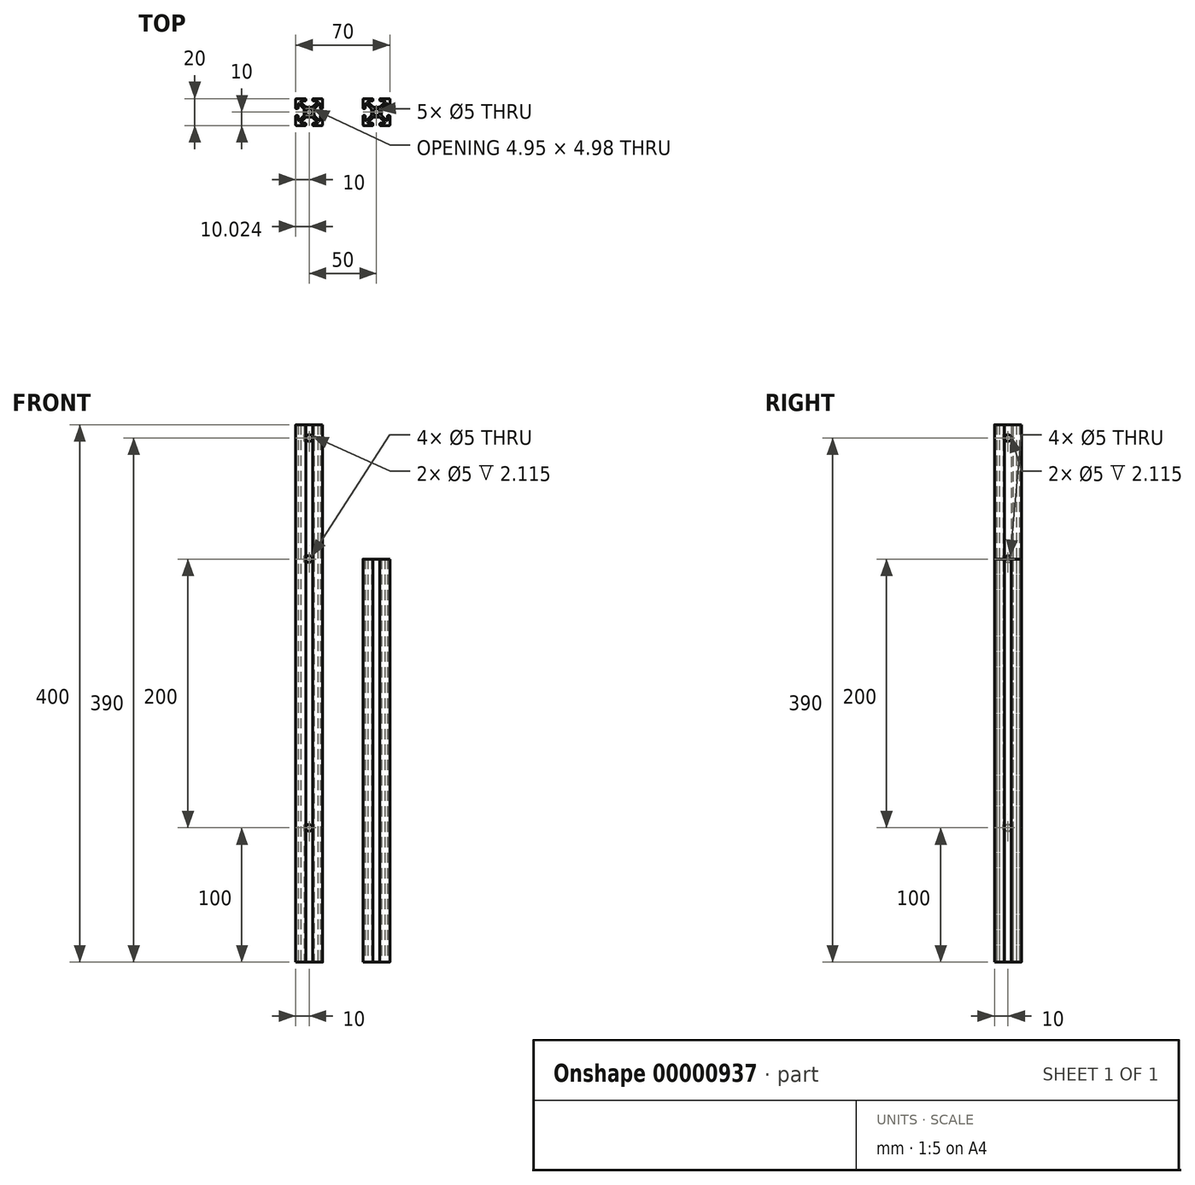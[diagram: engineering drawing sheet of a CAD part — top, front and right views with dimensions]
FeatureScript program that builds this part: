
annotation { "Feature Type Name" : "Feature", "Feature Type Description" : "" }
export const myFeature = defineFeature(function(context is Context, id is Id, definition is map)
    precondition{}
    {
        {
            var Q0;
            Q0=qCreatedBy(makeId("Top.planeOp"),FACE);
            var sketch = newSketch(context, id + "F0", { "sketchPlane" : qUnion([Q0])});
            skCircle(sketch, "E0", {"center": v(0, 0) * mm, "radius": 2.5 * mm});
            skLineSegment(sketch, "E1.bottom", {"start": v(-10, 10) * mm, "end": v(10, 10) * mm, "construction": true});
            skLineSegment(sketch, "E1.top", {"start": v(-10, -10) * mm, "end": v(10, -10) * mm, "construction": true});
            skLineSegment(sketch, "E1.left", {"start": v(-10, 10) * mm, "end": v(-10, -10) * mm, "construction": true});
            skLineSegment(sketch, "E1.right", {"start": v(10, 10) * mm, "end": v(10, -10) * mm, "construction": true});
            skLineSegment(sketch, "E2", {"start": v(-10, 10) * mm, "end": v(10, -10) * mm, "construction": true});
            skLineSegment(sketch, "E3", {"start": v(10, 10) * mm, "end": v(-10, -10) * mm, "construction": true});
            skLineSegment(sketch, "E4.rect.bottom", {"start": v(3.7, -3.7) * mm, "end": v(-3.7, -3.7) * mm, "construction": true});
            skLineSegment(sketch, "E4.rect.top", {"start": v(3.7, 3.7) * mm, "end": v(-3.7, 3.7) * mm, "construction": true});
            skLineSegment(sketch, "E4.rect.left", {"start": v(3.7, -3.7) * mm, "end": v(3.7, 3.7) * mm, "construction": true});
            skLineSegment(sketch, "E4.rect.right", {"start": v(-3.7, -3.7) * mm, "end": v(-3.7, 3.7) * mm, "construction": true});
            skLineSegment(sketch, "E5.rect.bottom", {"start": v(8.3, -8.3) * mm, "end": v(-8.3, -8.3) * mm, "construction": true});
            skLineSegment(sketch, "E5.rect.left", {"start": v(8.3, -8.3) * mm, "end": v(8.3, 8.3) * mm, "construction": true});
            skLineSegment(sketch, "E5.rect.right", {"start": v(-8.3, -8.3) * mm, "end": v(-8.3, 8.3) * mm, "construction": true});
            skLineSegment(sketch, "E6.rect.bottom", {"start": v(-2.5, 10) * mm, "end": v(2.5, 10) * mm, "construction": true});
            skLineSegment(sketch, "E6.rect.top", {"start": v(-2.5, -10) * mm, "end": v(2.5, -10) * mm, "construction": true});
            skLineSegment(sketch, "E6.rect.left", {"start": v(-2.5, 10) * mm, "end": v(-2.5, -10) * mm, "construction": true});
            skLineSegment(sketch, "E6.rect.right", {"start": v(2.5, 10) * mm, "end": v(2.5, -10) * mm, "construction": true});
            skLineSegment(sketch, "E7.rect.bottom", {"start": v(10, 2.5) * mm, "end": v(-10, 2.5) * mm, "construction": true});
            skLineSegment(sketch, "E7.rect.top", {"start": v(10, -2.5) * mm, "end": v(-10, -2.5) * mm, "construction": true});
            skLineSegment(sketch, "E7.rect.left", {"start": v(10, 2.5) * mm, "end": v(10, -2.5) * mm, "construction": true});
            skLineSegment(sketch, "E7.rect.right", {"start": v(-10, 2.5) * mm, "end": v(-10, -2.5) * mm, "construction": true});
            skLineSegment(sketch, "E8", {"start": v(-8.3, -7.1) * mm, "end": v(7.1, 8.3) * mm, "construction": true});
            skLineSegment(sketch, "E9", {"start": v(7.1, 8.3) * mm, "end": v(8.3, 7.1) * mm, "construction": true});
            skLineSegment(sketch, "E10", {"start": v(8.3, 7.1) * mm, "end": v(-7.1, -8.3) * mm, "construction": true});
            skLineSegment(sketch, "E11", {"start": v(-7.1, -8.3) * mm, "end": v(-8.3, -7.1) * mm, "construction": true});
            skLineSegment(sketch, "E12", {"start": v(-8.3, 7.1) * mm, "end": v(7.1, -8.3) * mm, "construction": true});
            skLineSegment(sketch, "E13", {"start": v(7.1, -8.3) * mm, "end": v(8.3, -7.1) * mm, "construction": true});
            skLineSegment(sketch, "E14", {"start": v(8.3, -7.1) * mm, "end": v(-7.1, 8.3) * mm, "construction": true});
            skLineSegment(sketch, "E15", {"start": v(-7.1, 8.3) * mm, "end": v(-8.3, 7.1) * mm, "construction": true});
            skLineSegment(sketch, "E16", {"start": v(-9.5, 2.5) * mm, "end": v(-8.8, 2.5) * mm});
            skLineSegment(sketch, "E17", {"start": v(-7.45, 6.24) * mm, "end": v(-4.29, 3.09) * mm});
            skLineSegment(sketch, "E18", {"start": v(-3.7, 1.67) * mm, "end": v(-3.7, -1.67) * mm});
            skLineSegment(sketch, "E19", {"start": v(-4.29, -3.08) * mm, "end": v(-7.45, -6.24) * mm});
            skLineSegment(sketch, "E20", {"start": v(-8.8, -2.5) * mm, "end": v(-9.5, -2.5) * mm});
            skLineSegment(sketch, "E21", {"start": v(-8.3, 3) * mm, "end": v(-8.3, 5.9) * mm});
            skLineSegment(sketch, "E22", {"start": v(-8.3, -5.9) * mm, "end": v(-8.3, -3) * mm});
            skLineSegment(sketch, "E23", {"start": v(-10, -3) * mm, "end": v(-10, -9.5) * mm});
            skLineSegment(sketch, "E24", {"start": v(-9.5, -10) * mm, "end": v(-3, -10) * mm});
            skLineSegment(sketch, "E25", {"start": v(-2.5, -9.5) * mm, "end": v(-2.5, -8.8) * mm});
            skLineSegment(sketch, "E26", {"start": v(-3, -8.3) * mm, "end": v(-5.89, -8.3) * mm});
            skLineSegment(sketch, "E27", {"start": v(-6.24, -7.45) * mm, "end": v(-3.09, -4.29) * mm});
            skLineSegment(sketch, "E28", {"start": v(-1.67, -3.7) * mm, "end": v(1.67, -3.7) * mm});
            skLineSegment(sketch, "E29", {"start": v(3.09, -4.29) * mm, "end": v(6.24, -7.45) * mm});
            skLineSegment(sketch, "E30", {"start": v(5.89, -8.3) * mm, "end": v(3, -8.3) * mm});
            skLineSegment(sketch, "E31", {"start": v(2.5, -8.8) * mm, "end": v(2.5, -9.5) * mm});
            skLineSegment(sketch, "E32", {"start": v(3, -10) * mm, "end": v(9.5, -10) * mm});
            skLineSegment(sketch, "E33", {"start": v(10, -9.5) * mm, "end": v(10, -3) * mm});
            skLineSegment(sketch, "E34", {"start": v(9.5, -2.5) * mm, "end": v(8.8, -2.5) * mm});
            skLineSegment(sketch, "E35", {"start": v(8.3, -3) * mm, "end": v(8.3, -5.89) * mm});
            skLineSegment(sketch, "E36", {"start": v(7.45, -6.24) * mm, "end": v(4.29, -3.09) * mm});
            skLineSegment(sketch, "E37", {"start": v(3.7, -1.67) * mm, "end": v(3.7, 1.67) * mm});
            skLineSegment(sketch, "E38", {"start": v(4.29, 3.09) * mm, "end": v(7.45, 6.24) * mm});
            skLineSegment(sketch, "E39", {"start": v(8.3, 5.89) * mm, "end": v(8.3, 3) * mm});
            skLineSegment(sketch, "E40", {"start": v(8.8, 2.5) * mm, "end": v(9.5, 2.5) * mm});
            skLineSegment(sketch, "E41", {"start": v(10, 3) * mm, "end": v(10, 9.5) * mm});
            skLineSegment(sketch, "E42", {"start": v(9.5, 10) * mm, "end": v(3, 10) * mm});
            skLineSegment(sketch, "E43", {"start": v(2.5, 9.5) * mm, "end": v(2.5, 8.8) * mm});
            skLineSegment(sketch, "E44", {"start": v(3, 8.3) * mm, "end": v(5.89, 8.3) * mm});
            skLineSegment(sketch, "E45", {"start": v(6.24, 7.45) * mm, "end": v(3.09, 4.29) * mm});
            skLineSegment(sketch, "E46", {"start": v(1.67, 3.7) * mm, "end": v(-1.67, 3.7) * mm});
            skLineSegment(sketch, "E47", {"start": v(-3.09, 4.29) * mm, "end": v(-6.24, 7.45) * mm});
            skLineSegment(sketch, "E48", {"start": v(-5.89, 8.3) * mm, "end": v(-3, 8.3) * mm});
            skLineSegment(sketch, "E49", {"start": v(-2.5, 8.8) * mm, "end": v(-2.5, 9.5) * mm});
            skLineSegment(sketch, "E50", {"start": v(-3, 10) * mm, "end": v(-9.5, 10) * mm});
            skLineSegment(sketch, "E51", {"start": v(-10, 9.5) * mm, "end": v(-10, 3) * mm});
            skPoint(sketch, "E52.visualSharp", {"position": v(-7.1, 8.3) * mm});
            skArc(sketch, "E52.filletArc", {"start": v(-5.89, 8.3) * mm, "mid": v(-6.35, 8) * mm, "end": v(-6.24, 7.45) * mm});
            skPoint(sketch, "E53.visualSharp", {"position": v(-8.3, 7.1) * mm});
            skArc(sketch, "E53.filletArc", {"start": v(-7.45, 6.24) * mm, "mid": v(-8, 6.35) * mm, "end": v(-8.3, 5.9) * mm});
            skPoint(sketch, "E54.visualSharp", {"position": v(-8.3, -7.1) * mm});
            skArc(sketch, "E54.filletArc", {"start": v(-8.3, -5.9) * mm, "mid": v(-8, -6.35) * mm, "end": v(-7.45, -6.24) * mm});
            skPoint(sketch, "E55.visualSharp", {"position": v(-7.1, -8.3) * mm});
            skArc(sketch, "E55.filletArc", {"start": v(-6.24, -7.45) * mm, "mid": v(-6.35, -8) * mm, "end": v(-5.89, -8.3) * mm});
            skPoint(sketch, "E56.visualSharp", {"position": v(7.1, -8.3) * mm});
            skArc(sketch, "E56.filletArc", {"start": v(5.89, -8.3) * mm, "mid": v(6.35, -8) * mm, "end": v(6.24, -7.45) * mm});
            skPoint(sketch, "E57.visualSharp", {"position": v(8.3, -7.1) * mm});
            skArc(sketch, "E57.filletArc", {"start": v(7.45, -6.24) * mm, "mid": v(8, -6.35) * mm, "end": v(8.3, -5.89) * mm});
            skPoint(sketch, "E58.visualSharp", {"position": v(8.3, 7.1) * mm});
            skArc(sketch, "E58.filletArc", {"start": v(8.3, 5.89) * mm, "mid": v(8, 6.35) * mm, "end": v(7.45, 6.24) * mm});
            skPoint(sketch, "E59.visualSharp", {"position": v(7.1, 8.3) * mm});
            skArc(sketch, "E59.filletArc", {"start": v(6.24, 7.45) * mm, "mid": v(6.35, 8) * mm, "end": v(5.89, 8.3) * mm});
            skPoint(sketch, "E60.visualSharp", {"position": v(-10, 10) * mm});
            skArc(sketch, "E60.filletArc", {"start": v(-9.5, 10) * mm, "mid": v(-9.85, 9.85) * mm, "end": v(-10, 9.5) * mm});
            skPoint(sketch, "E61.visualSharp", {"position": v(10, 10) * mm});
            skArc(sketch, "E61.filletArc", {"start": v(10, 9.5) * mm, "mid": v(9.85, 9.85) * mm, "end": v(9.5, 10) * mm});
            skPoint(sketch, "E62.visualSharp", {"position": v(10, -10) * mm});
            skArc(sketch, "E62.filletArc", {"start": v(9.5, -10) * mm, "mid": v(9.85, -9.85) * mm, "end": v(10, -9.5) * mm});
            skPoint(sketch, "E63.visualSharp", {"position": v(-10, -10) * mm});
            skArc(sketch, "E63.filletArc", {"start": v(-10, -9.5) * mm, "mid": v(-9.85, -9.85) * mm, "end": v(-9.5, -10) * mm});
            skPoint(sketch, "E64.visualSharp", {"position": v(-10, 2.5) * mm});
            skArc(sketch, "E64.filletArc", {"start": v(-10, 3) * mm, "mid": v(-9.85, 2.65) * mm, "end": v(-9.5, 2.5) * mm});
            skPoint(sketch, "E65.visualSharp", {"position": v(-2.5, 8.3) * mm});
            skArc(sketch, "E65.filletArc", {"start": v(-3, 8.3) * mm, "mid": v(-2.65, 8.45) * mm, "end": v(-2.5, 8.8) * mm});
            skPoint(sketch, "E66.visualSharp", {"position": v(-8.3, -2.5) * mm});
            skArc(sketch, "E66.filletArc", {"start": v(-8.3, -3) * mm, "mid": v(-8.45, -2.65) * mm, "end": v(-8.8, -2.5) * mm});
            skPoint(sketch, "E67.visualSharp", {"position": v(-2.5, 10) * mm});
            skArc(sketch, "E67.filletArc", {"start": v(-2.5, 9.5) * mm, "mid": v(-2.65, 9.85) * mm, "end": v(-3, 10) * mm});
            skPoint(sketch, "E68.visualSharp", {"position": v(2.5, 10) * mm});
            skArc(sketch, "E68.filletArc", {"start": v(3, 10) * mm, "mid": v(2.65, 9.85) * mm, "end": v(2.5, 9.5) * mm});
            skPoint(sketch, "E69.visualSharp", {"position": v(2.5, 8.3) * mm});
            skArc(sketch, "E69.filletArc", {"start": v(2.5, 8.8) * mm, "mid": v(2.65, 8.45) * mm, "end": v(3, 8.3) * mm});
            skPoint(sketch, "E70.visualSharp", {"position": v(8.3, 2.5) * mm});
            skArc(sketch, "E70.filletArc", {"start": v(8.3, 3) * mm, "mid": v(8.45, 2.65) * mm, "end": v(8.8, 2.5) * mm});
            skPoint(sketch, "E71.visualSharp", {"position": v(10, 2.5) * mm});
            skArc(sketch, "E71.filletArc", {"start": v(9.5, 2.5) * mm, "mid": v(9.85, 2.65) * mm, "end": v(10, 3) * mm});
            skPoint(sketch, "E72.visualSharp", {"position": v(8.3, -2.5) * mm});
            skArc(sketch, "E72.filletArc", {"start": v(8.8, -2.5) * mm, "mid": v(8.45, -2.65) * mm, "end": v(8.3, -3) * mm});
            skPoint(sketch, "E73.visualSharp", {"position": v(10, -2.5) * mm});
            skArc(sketch, "E73.filletArc", {"start": v(10, -3) * mm, "mid": v(9.85, -2.65) * mm, "end": v(9.5, -2.5) * mm});
            skPoint(sketch, "E74.visualSharp", {"position": v(2.5, -8.3) * mm});
            skArc(sketch, "E74.filletArc", {"start": v(3, -8.3) * mm, "mid": v(2.65, -8.45) * mm, "end": v(2.5, -8.8) * mm});
            skPoint(sketch, "E75.visualSharp", {"position": v(-2.5, -8.3) * mm});
            skArc(sketch, "E75.filletArc", {"start": v(-2.5, -8.8) * mm, "mid": v(-2.65, -8.45) * mm, "end": v(-3, -8.3) * mm});
            skPoint(sketch, "E76.visualSharp", {"position": v(2.5, -10) * mm});
            skArc(sketch, "E76.filletArc", {"start": v(2.5, -9.5) * mm, "mid": v(2.65, -9.85) * mm, "end": v(3, -10) * mm});
            skPoint(sketch, "E77.visualSharp", {"position": v(-2.5, -10) * mm});
            skArc(sketch, "E77.filletArc", {"start": v(-3, -10) * mm, "mid": v(-2.65, -9.85) * mm, "end": v(-2.5, -9.5) * mm});
            skPoint(sketch, "E78.visualSharp", {"position": v(-10, -2.5) * mm});
            skArc(sketch, "E78.filletArc", {"start": v(-9.5, -2.5) * mm, "mid": v(-9.85, -2.65) * mm, "end": v(-10, -3) * mm});
            skPoint(sketch, "E79.visualSharp", {"position": v(-8.3, 2.5) * mm});
            skArc(sketch, "E79.filletArc", {"start": v(-8.8, 2.5) * mm, "mid": v(-8.45, 2.65) * mm, "end": v(-8.3, 3) * mm});
            skPoint(sketch, "E80.visualSharp", {"position": v(-3.7, 2.5) * mm});
            skArc(sketch, "E80.filletArc", {"start": v(-3.7, 1.67) * mm, "mid": v(-3.85, 2.44) * mm, "end": v(-4.29, 3.09) * mm});
            skPoint(sketch, "E81.visualSharp", {"position": v(-2.5, 3.7) * mm});
            skArc(sketch, "E81.filletArc", {"start": v(-3.09, 4.29) * mm, "mid": v(-2.44, 3.85) * mm, "end": v(-1.67, 3.7) * mm});
            skPoint(sketch, "E82.visualSharp", {"position": v(2.5, 3.7) * mm});
            skArc(sketch, "E82.filletArc", {"start": v(1.67, 3.7) * mm, "mid": v(2.44, 3.85) * mm, "end": v(3.09, 4.29) * mm});
            skPoint(sketch, "E83.visualSharp", {"position": v(3.7, 2.5) * mm});
            skArc(sketch, "E83.filletArc", {"start": v(4.29, 3.09) * mm, "mid": v(3.85, 2.44) * mm, "end": v(3.7, 1.67) * mm});
            skPoint(sketch, "E84.visualSharp", {"position": v(3.7, -2.5) * mm});
            skArc(sketch, "E84.filletArc", {"start": v(3.7, -1.67) * mm, "mid": v(3.85, -2.44) * mm, "end": v(4.29, -3.09) * mm});
            skPoint(sketch, "E85.visualSharp", {"position": v(2.5, -3.7) * mm});
            skArc(sketch, "E85.filletArc", {"start": v(3.09, -4.29) * mm, "mid": v(2.44, -3.85) * mm, "end": v(1.67, -3.7) * mm});
            skPoint(sketch, "E86.visualSharp", {"position": v(-2.5, -3.7) * mm});
            skArc(sketch, "E86.filletArc", {"start": v(-1.67, -3.7) * mm, "mid": v(-2.44, -3.85) * mm, "end": v(-3.09, -4.29) * mm});
            skPoint(sketch, "E87.visualSharp", {"position": v(-3.7, -2.5) * mm});
            skArc(sketch, "E87.filletArc", {"start": v(-4.29, -3.08) * mm, "mid": v(-3.85, -2.43) * mm, "end": v(-3.7, -1.67) * mm});
            skLineSegment(sketch, "E88", {"start": v(-8.3, 8.3) * mm, "end": v(8.3, 8.3) * mm, "construction": true});
            skSolve(sketch);
        }
        {
            var Q0;
            Q0=makeQuery(id+"F0.imprint","IMPRINT",FACE,{"disambiguationData":[TD([[makeQuery(id+"F0.imprint","IMPRINT",EDGE,{"derivedFrom":sQuery(id+"F0.wireOp",EDGE,"E0")}),-1.0]])]});
            extrude(context, id + "F1", {"entities" : qUnion([Q0]), "depth" : 300 * mm});
        }
        {
            var Q0;
            Q0=makeQuery(id+"F1.opExtrude","SWEPT_BODY",BODY,{"disambiguationData":[OSD([sQuery(id+"F0.wireOp",EDGE,"E0"),sQuery(id+"F0.wireOp",EDGE,"E16"),sQuery(id+"F0.wireOp",EDGE,"E17"),sQuery(id+"F0.wireOp",EDGE,"E18"),sQuery(id+"F0.wireOp",EDGE,"E19"),sQuery(id+"F0.wireOp",EDGE,"E20"),sQuery(id+"F0.wireOp",EDGE,"E21"),sQuery(id+"F0.wireOp",EDGE,"E22"),sQuery(id+"F0.wireOp",EDGE,"E23"),sQuery(id+"F0.wireOp",EDGE,"E24"),sQuery(id+"F0.wireOp",EDGE,"E25"),sQuery(id+"F0.wireOp",EDGE,"E26"),sQuery(id+"F0.wireOp",EDGE,"E27"),sQuery(id+"F0.wireOp",EDGE,"E28"),sQuery(id+"F0.wireOp",EDGE,"E29"),sQuery(id+"F0.wireOp",EDGE,"E30"),sQuery(id+"F0.wireOp",EDGE,"E31"),sQuery(id+"F0.wireOp",EDGE,"E32"),sQuery(id+"F0.wireOp",EDGE,"E33"),sQuery(id+"F0.wireOp",EDGE,"E34"),sQuery(id+"F0.wireOp",EDGE,"E35"),sQuery(id+"F0.wireOp",EDGE,"E36"),sQuery(id+"F0.wireOp",EDGE,"E37"),sQuery(id+"F0.wireOp",EDGE,"E38"),sQuery(id+"F0.wireOp",EDGE,"E39"),sQuery(id+"F0.wireOp",EDGE,"E40"),sQuery(id+"F0.wireOp",EDGE,"E41"),sQuery(id+"F0.wireOp",EDGE,"E42"),sQuery(id+"F0.wireOp",EDGE,"E43"),sQuery(id+"F0.wireOp",EDGE,"E44"),sQuery(id+"F0.wireOp",EDGE,"E45"),sQuery(id+"F0.wireOp",EDGE,"E46"),sQuery(id+"F0.wireOp",EDGE,"E47"),sQuery(id+"F0.wireOp",EDGE,"E48"),sQuery(id+"F0.wireOp",EDGE,"E49"),sQuery(id+"F0.wireOp",EDGE,"E50"),sQuery(id+"F0.wireOp",EDGE,"E51"),sQuery(id+"F0.wireOp",EDGE,"E52.filletArc"),sQuery(id+"F0.wireOp",EDGE,"E53.filletArc"),sQuery(id+"F0.wireOp",EDGE,"E54.filletArc"),sQuery(id+"F0.wireOp",EDGE,"E55.filletArc"),sQuery(id+"F0.wireOp",EDGE,"E56.filletArc"),sQuery(id+"F0.wireOp",EDGE,"E57.filletArc"),sQuery(id+"F0.wireOp",EDGE,"E58.filletArc"),sQuery(id+"F0.wireOp",EDGE,"E59.filletArc"),sQuery(id+"F0.wireOp",EDGE,"E60.filletArc"),sQuery(id+"F0.wireOp",EDGE,"E61.filletArc"),sQuery(id+"F0.wireOp",EDGE,"E62.filletArc"),sQuery(id+"F0.wireOp",EDGE,"E63.filletArc"),sQuery(id+"F0.wireOp",EDGE,"E64.filletArc"),sQuery(id+"F0.wireOp",EDGE,"E65.filletArc"),sQuery(id+"F0.wireOp",EDGE,"E66.filletArc"),sQuery(id+"F0.wireOp",EDGE,"E67.filletArc"),sQuery(id+"F0.wireOp",EDGE,"E68.filletArc"),sQuery(id+"F0.wireOp",EDGE,"E69.filletArc"),sQuery(id+"F0.wireOp",EDGE,"E70.filletArc"),sQuery(id+"F0.wireOp",EDGE,"E71.filletArc"),sQuery(id+"F0.wireOp",EDGE,"E72.filletArc"),sQuery(id+"F0.wireOp",EDGE,"E73.filletArc"),sQuery(id+"F0.wireOp",EDGE,"E74.filletArc"),sQuery(id+"F0.wireOp",EDGE,"E75.filletArc"),sQuery(id+"F0.wireOp",EDGE,"E76.filletArc"),sQuery(id+"F0.wireOp",EDGE,"E77.filletArc"),sQuery(id+"F0.wireOp",EDGE,"E78.filletArc"),sQuery(id+"F0.wireOp",EDGE,"E79.filletArc"),sQuery(id+"F0.wireOp",EDGE,"E80.filletArc"),sQuery(id+"F0.wireOp",EDGE,"E81.filletArc"),sQuery(id+"F0.wireOp",EDGE,"E82.filletArc"),sQuery(id+"F0.wireOp",EDGE,"E83.filletArc"),sQuery(id+"F0.wireOp",EDGE,"E84.filletArc"),sQuery(id+"F0.wireOp",EDGE,"E85.filletArc"),sQuery(id+"F0.wireOp",EDGE,"E86.filletArc"),sQuery(id+"F0.wireOp",EDGE,"E87.filletArc")])]});
            transform(context, id + "F2", {"entities" : qUnion([Q0]), "transformType" : TransformType.TRANSLATION_3D, "dx" : -50 * mm, "dy" : 0 * mm, "dz" : 0 * mm, "makeCopy" : true});
        }
        {
            var Q0;
            Q0=makeQuery(id+"F2.opPattern","COPY",FACE,{"derivedFrom":makeQuery(id+"F1.opExtrude","CAP_FACE",FACE,{"disambiguationData":[OSD([sQuery(id+"F0.wireOp",EDGE,"E0"),sQuery(id+"F0.wireOp",EDGE,"E16"),sQuery(id+"F0.wireOp",EDGE,"E17"),sQuery(id+"F0.wireOp",EDGE,"E18"),sQuery(id+"F0.wireOp",EDGE,"E19"),sQuery(id+"F0.wireOp",EDGE,"E20"),sQuery(id+"F0.wireOp",EDGE,"E21"),sQuery(id+"F0.wireOp",EDGE,"E22"),sQuery(id+"F0.wireOp",EDGE,"E23"),sQuery(id+"F0.wireOp",EDGE,"E24"),sQuery(id+"F0.wireOp",EDGE,"E25"),sQuery(id+"F0.wireOp",EDGE,"E26"),sQuery(id+"F0.wireOp",EDGE,"E27"),sQuery(id+"F0.wireOp",EDGE,"E28"),sQuery(id+"F0.wireOp",EDGE,"E29"),sQuery(id+"F0.wireOp",EDGE,"E30"),sQuery(id+"F0.wireOp",EDGE,"E31"),sQuery(id+"F0.wireOp",EDGE,"E32"),sQuery(id+"F0.wireOp",EDGE,"E33"),sQuery(id+"F0.wireOp",EDGE,"E34"),sQuery(id+"F0.wireOp",EDGE,"E35"),sQuery(id+"F0.wireOp",EDGE,"E36"),sQuery(id+"F0.wireOp",EDGE,"E37"),sQuery(id+"F0.wireOp",EDGE,"E38"),sQuery(id+"F0.wireOp",EDGE,"E39"),sQuery(id+"F0.wireOp",EDGE,"E40"),sQuery(id+"F0.wireOp",EDGE,"E41"),sQuery(id+"F0.wireOp",EDGE,"E42"),sQuery(id+"F0.wireOp",EDGE,"E43"),sQuery(id+"F0.wireOp",EDGE,"E44"),sQuery(id+"F0.wireOp",EDGE,"E45"),sQuery(id+"F0.wireOp",EDGE,"E46"),sQuery(id+"F0.wireOp",EDGE,"E47"),sQuery(id+"F0.wireOp",EDGE,"E48"),sQuery(id+"F0.wireOp",EDGE,"E49"),sQuery(id+"F0.wireOp",EDGE,"E50"),sQuery(id+"F0.wireOp",EDGE,"E51"),sQuery(id+"F0.wireOp",EDGE,"E52.filletArc"),sQuery(id+"F0.wireOp",EDGE,"E53.filletArc"),sQuery(id+"F0.wireOp",EDGE,"E54.filletArc"),sQuery(id+"F0.wireOp",EDGE,"E55.filletArc"),sQuery(id+"F0.wireOp",EDGE,"E56.filletArc"),sQuery(id+"F0.wireOp",EDGE,"E57.filletArc"),sQuery(id+"F0.wireOp",EDGE,"E58.filletArc"),sQuery(id+"F0.wireOp",EDGE,"E59.filletArc"),sQuery(id+"F0.wireOp",EDGE,"E60.filletArc"),sQuery(id+"F0.wireOp",EDGE,"E61.filletArc"),sQuery(id+"F0.wireOp",EDGE,"E62.filletArc"),sQuery(id+"F0.wireOp",EDGE,"E63.filletArc"),sQuery(id+"F0.wireOp",EDGE,"E64.filletArc"),sQuery(id+"F0.wireOp",EDGE,"E65.filletArc"),sQuery(id+"F0.wireOp",EDGE,"E66.filletArc"),sQuery(id+"F0.wireOp",EDGE,"E67.filletArc"),sQuery(id+"F0.wireOp",EDGE,"E68.filletArc"),sQuery(id+"F0.wireOp",EDGE,"E69.filletArc"),sQuery(id+"F0.wireOp",EDGE,"E70.filletArc"),sQuery(id+"F0.wireOp",EDGE,"E71.filletArc"),sQuery(id+"F0.wireOp",EDGE,"E72.filletArc"),sQuery(id+"F0.wireOp",EDGE,"E73.filletArc"),sQuery(id+"F0.wireOp",EDGE,"E74.filletArc"),sQuery(id+"F0.wireOp",EDGE,"E75.filletArc"),sQuery(id+"F0.wireOp",EDGE,"E76.filletArc"),sQuery(id+"F0.wireOp",EDGE,"E77.filletArc"),sQuery(id+"F0.wireOp",EDGE,"E78.filletArc"),sQuery(id+"F0.wireOp",EDGE,"E79.filletArc"),sQuery(id+"F0.wireOp",EDGE,"E80.filletArc"),sQuery(id+"F0.wireOp",EDGE,"E81.filletArc"),sQuery(id+"F0.wireOp",EDGE,"E82.filletArc"),sQuery(id+"F0.wireOp",EDGE,"E83.filletArc"),sQuery(id+"F0.wireOp",EDGE,"E84.filletArc"),sQuery(id+"F0.wireOp",EDGE,"E85.filletArc"),sQuery(id+"F0.wireOp",EDGE,"E86.filletArc"),sQuery(id+"F0.wireOp",EDGE,"E87.filletArc")])],"isStart":false}),"instanceName":"1"});
            extrude(context, id + "F3", {"entities" : qUnion([Q0]), "operationType" : NewBodyOperationType.ADD, "depth" : 100 * mm});
        }
        {
            var Q0;
            {var subQ0=sQuery(id+"F0.wireOp",EDGE,"E24");Q0=makeQuery(id+"F3.boolean.opBoolean","MERGE",FACE,{"derivedFrom":[makeQuery(id+"F2.opPattern","COPY",FACE,{"derivedFrom":makeQuery(id+"F1.opExtrude","SWEPT_FACE",FACE,{"disambiguationData":[OSD([subQ0])]}),"instanceName":"1"}),makeQuery(id+"F3.opExtrude","SWEPT_FACE",FACE,{"disambiguationData":[OSD([subQ0])]})]});}
            var sketch = newSketch(context, id + "F4", { "sketchPlane" : qUnion([Q0])});
            skCircle(sketch, "E89", {"center": v(-50, 300) * mm, "radius": 2.5 * mm});
            skCircle(sketch, "E90", {"center": v(-50, 100) * mm, "radius": 2.5 * mm});
            skLineSegment(sketch, "E91", {"start": v(-48.33, 100) * mm, "end": v(-51.67, 100) * mm, "construction": true});
            skLineSegment(sketch, "E92", {"start": v(-51.67, 300) * mm, "end": v(-48.33, 300) * mm, "construction": true});
            skLineSegment(sketch, "E93", {"start": v(-48.33, 390) * mm, "end": v(-51.67, 390) * mm, "construction": true});
            skCircle(sketch, "E94", {"center": v(-50, 390) * mm, "radius": 2.5 * mm});
            skSolve(sketch);
        }
        {
            var Q0;
            Q0 = qSketchRegion(id + "F4", true);
            extrude(context, id + "F5", {"entities" : qUnion([Q0]), "operationType" : NewBodyOperationType.REMOVE, "oppositeDirection" : true, "depth" : 25 * mm});
        }
        {
            var Q0;
            {var subQ0=sQuery(id+"F0.wireOp",EDGE,"E51");Q0=makeQuery(id+"F3.boolean.opBoolean","MERGE",FACE,{"derivedFrom":[makeQuery(id+"F2.opPattern","COPY",FACE,{"derivedFrom":makeQuery(id+"F1.opExtrude","SWEPT_FACE",FACE,{"disambiguationData":[OSD([subQ0])]}),"instanceName":"1"}),makeQuery(id+"F3.opExtrude","SWEPT_FACE",FACE,{"disambiguationData":[OSD([subQ0])]})]});}
            var sketch = newSketch(context, id + "F6", { "sketchPlane" : qUnion([Q0])});
            skLineSegment(sketch, "E95", {"start": v(-1.67, 390) * mm, "end": v(1.67, 390) * mm, "construction": true});
            skCircle(sketch, "E96", {"center": v(0, 390) * mm, "radius": 2.5 * mm});
            skLineSegment(sketch, "E97", {"start": v(-1.67, 100) * mm, "end": v(1.67, 100) * mm, "construction": true});
            skCircle(sketch, "E98", {"center": v(0, 100) * mm, "radius": 2.5 * mm});
            skCircle(sketch, "E99", {"center": v(0, 300) * mm, "radius": 2.5 * mm});
            skSolve(sketch);
        }
        {
            var Q0;
            Q0 = qSketchRegion(id + "F6", true);
            extrude(context, id + "F7", {"entities" : qUnion([Q0]), "operationType" : NewBodyOperationType.REMOVE, "oppositeDirection" : true, "depth" : 25 * mm});
        }
    });
